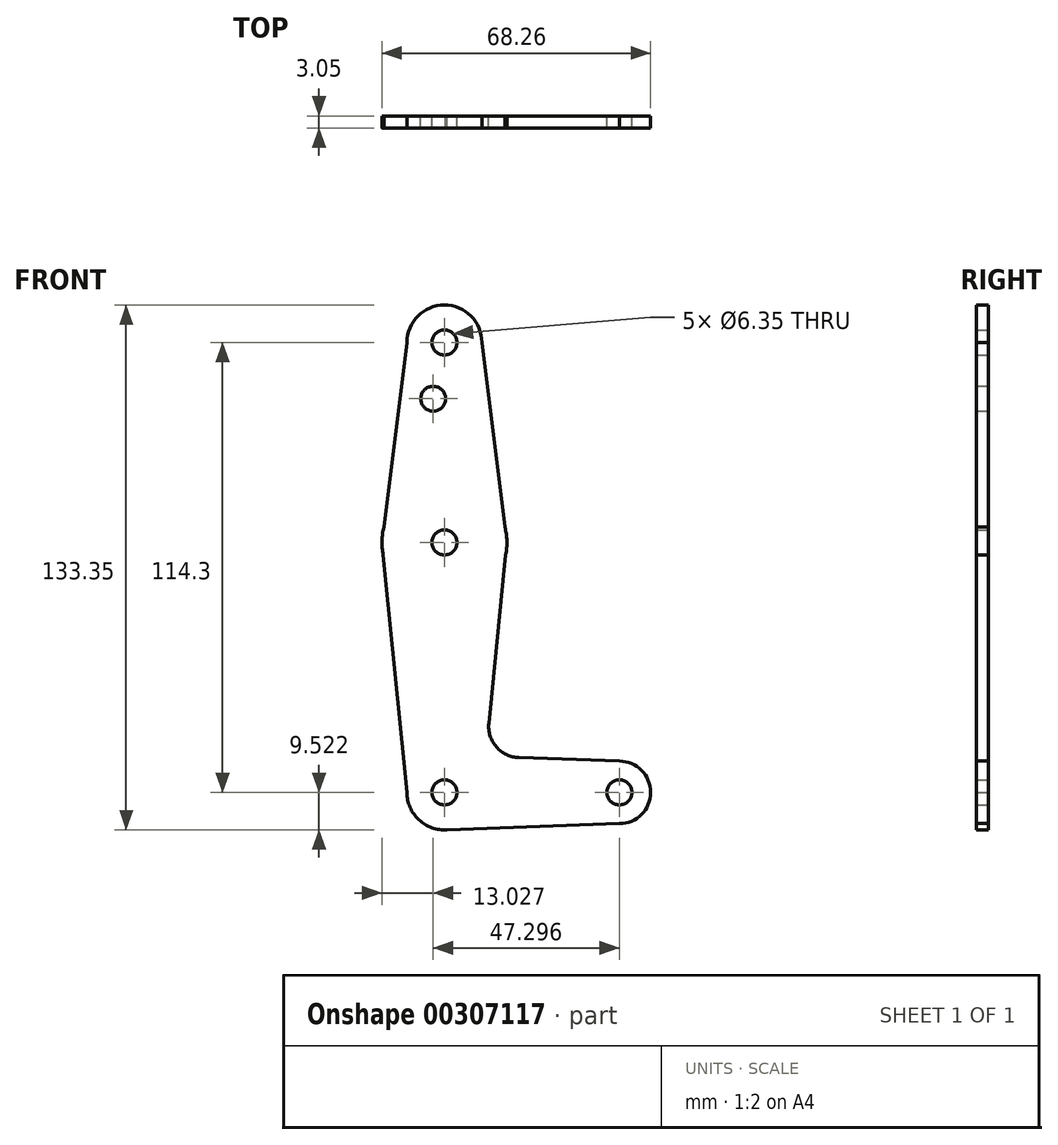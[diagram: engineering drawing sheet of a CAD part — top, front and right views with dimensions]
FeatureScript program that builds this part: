
annotation { "Feature Type Name" : "Feature", "Feature Type Description" : "" }
export const myFeature = defineFeature(function(context is Context, id is Id, definition is map)
    precondition{}
    {
        {
            var Q0;
            Q0=qCreatedBy(makeId("Front.planeOp"),FACE);
            var sketch = newSketch(context, id + "F0", { "sketchPlane" : qUnion([Q0])});
            skCircle(sketch, "E0", {"center": v(-56.36, 62.07) * mm, "radius": 9.53 * mm});
            skCircle(sketch, "E1", {"center": v(-56.36, 11.27) * mm, "radius": 15.88 * mm});
            skCircle(sketch, "E2", {"center": v(-56.36, -52.23) * mm, "radius": 9.53 * mm});
            skCircle(sketch, "E3", {"center": v(-11.9, -52.23) * mm, "radius": 7.94 * mm});
            skLineSegment(sketch, "E4", {"start": v(-56.36, 62.07) * mm, "end": v(-56.36, 11.27) * mm, "construction": true});
            skLineSegment(sketch, "E5", {"start": v(-56.36, 11.27) * mm, "end": v(-56.36, -52.23) * mm, "construction": true});
            skLineSegment(sketch, "E6", {"start": v(-56.36, -52.23) * mm, "end": v(-11.9, -52.23) * mm, "construction": true});
            skLineSegment(sketch, "E7", {"start": v(-65.88, 62.07) * mm, "end": v(-72.23, 11.27) * mm});
            skLineSegment(sketch, "E8", {"start": v(-72.23, 11.27) * mm, "end": v(-65.88, -52.23) * mm});
            skLineSegment(sketch, "E9", {"start": v(-46.83, 62.07) * mm, "end": v(-40.48, 11.27) * mm});
            skLineSegment(sketch, "E10", {"start": v(-56.36, -61.75) * mm, "end": v(-11.9, -60.17) * mm});
            skCircle(sketch, "E11", {"center": v(-56.36, 62.07) * mm, "radius": 3.18 * mm});
            skCircle(sketch, "E12", {"center": v(-56.36, 11.27) * mm, "radius": 3.18 * mm});
            skCircle(sketch, "E13", {"center": v(-56.36, -52.23) * mm, "radius": 3.17 * mm});
            skCircle(sketch, "E14", {"center": v(-11.9, -52.23) * mm, "radius": 3.18 * mm});
            skCircle(sketch, "E15", {"center": v(-59.2, 47.8) * mm, "radius": 3.17 * mm});
            skLineSegment(sketch, "E16", {"start": v(-56.36, -52.23) * mm, "end": v(-56.36, -42.7) * mm});
            skLineSegment(sketch, "E17", {"start": v(-56.36, 11.27) * mm, "end": v(-40.48, 11.27) * mm});
            skLineSegment(sketch, "E18", {"start": v(-40.48, 11.27) * mm, "end": v(-45.07, -34.64) * mm});
            skLineSegment(sketch, "E19", {"start": v(-37.45, -43.38) * mm, "end": v(-11.9, -44.3) * mm});
            skPoint(sketch, "E20.newPointB", {"position": v(-46.83, -52.23) * mm});
            skArc(sketch, "E20.filletArc", {"start": v(-45.07, -34.64) * mm, "mid": v(-43.15, -40.66) * mm, "end": v(-37.45, -43.38) * mm});
            skSolve(sketch);
        }
        {
            var Q0;
            Q0 = qSketchRegion(id + "F0", true);
            extrude(context, id + "F1", {"entities" : qUnion([Q0]), "depth" : 3.05 * mm});
        }
    });
